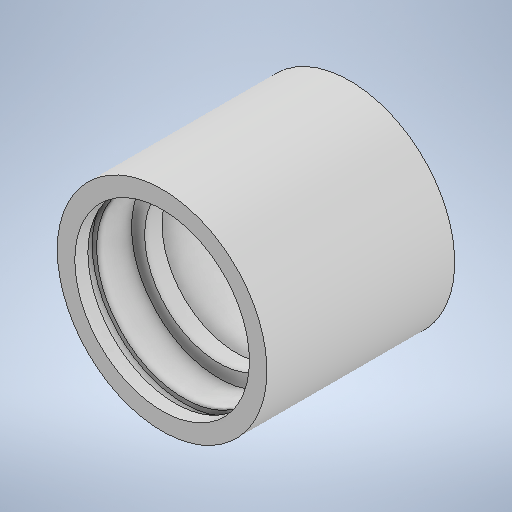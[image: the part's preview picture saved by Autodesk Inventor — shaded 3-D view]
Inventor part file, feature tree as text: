
AUTODESK INVENTOR PART (.ipt)
format: ipt  version: 2025 (Build 290162010, 162A)  size: 281,088 bytes
history: native  units: mm
features: other x1, revolve x1, sketch x1
ambient origin geometry x8: Origin, YZ Plane, XZ Plane, XY Plane, X Axis, Y Axis, Z Axis, Center Point
bodies: Body1 (feature_tree)
feature tree (3):
  other  "Седло для подшипника"
  revolve  "Revolution1"  [1 undecoded]
  sketch  "Sketch6"  dims[d15=4.0mm d16=3.0mm d17=8.0mm d18=2.0mm d19=1.0mm d20=360.0deg d21=48.0mm d22=40.0mm d24=14.0mm d25=15.0mm d26=2.0mm d27=1.0mm d28=28.0mm]
note: 1 required parameter value undecoded (feature->parameter linkage not recoverable at this tier; creation-order binding heuristic only, values carry confidence <= 0.55)
